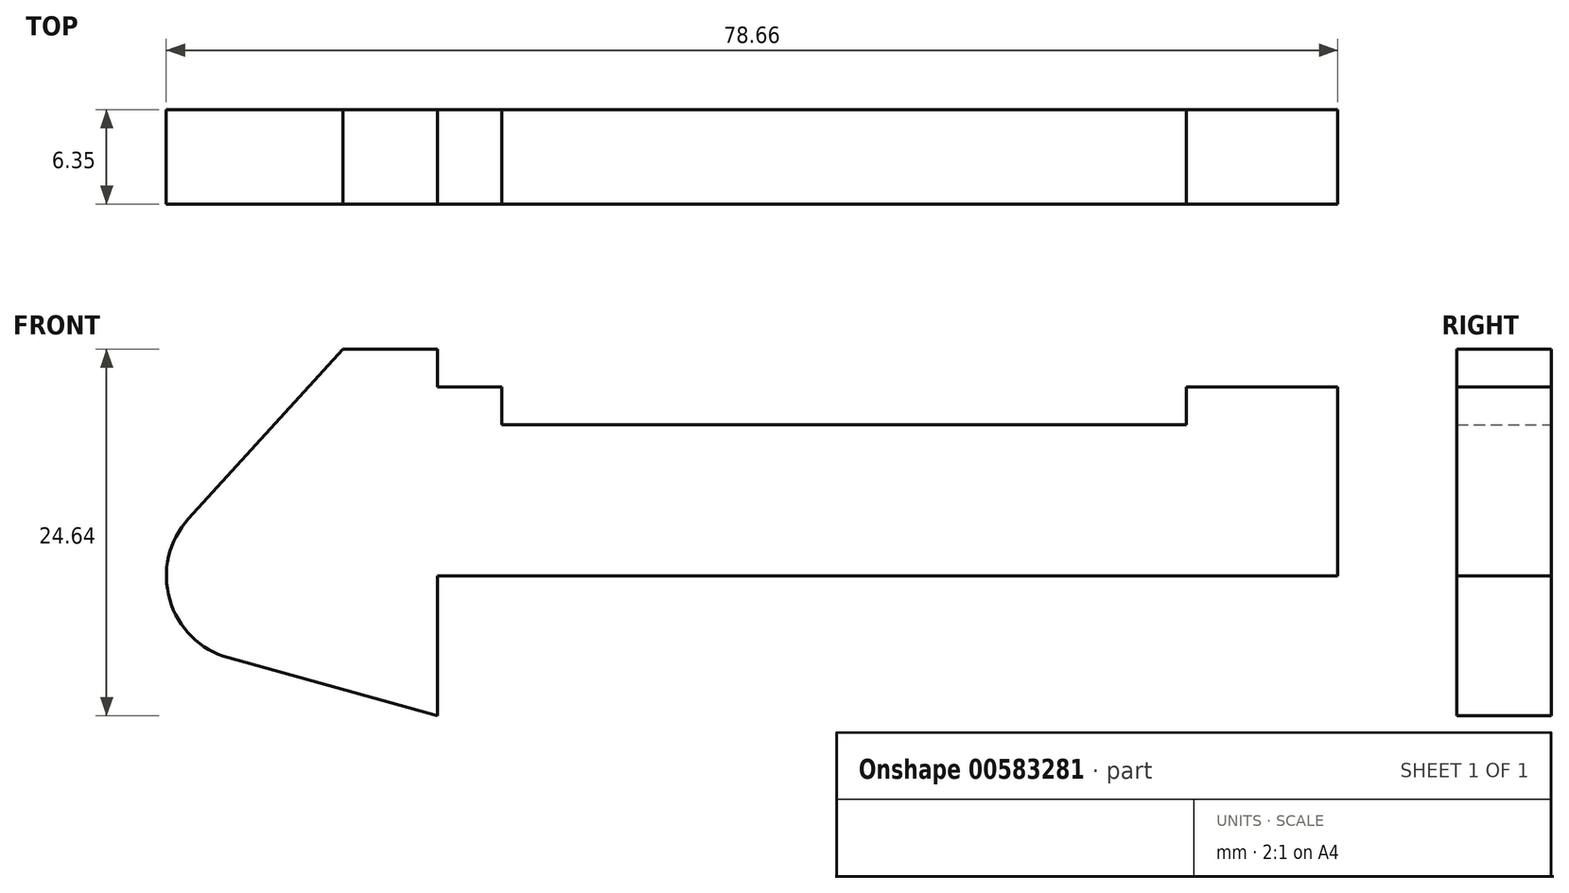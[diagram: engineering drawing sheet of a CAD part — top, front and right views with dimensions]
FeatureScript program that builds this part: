
annotation { "Feature Type Name" : "Feature", "Feature Type Description" : "" }
export const myFeature = defineFeature(function(context is Context, id is Id, definition is map)
    precondition{}
    {
        {
            var Q0;
            Q0=qCreatedBy(makeId("Front.planeOp"),FACE);
            var sketch = newSketch(context, id + "F0", { "sketchPlane" : qUnion([Q0])});
            skLineSegment(sketch, "E0", {"start": v(0, 0) * mm, "end": v(0, 12.7) * mm});
            skLineSegment(sketch, "E1", {"start": v(0, 12.7) * mm, "end": v(10.16, 12.7) * mm});
            skLineSegment(sketch, "E2", {"start": v(10.16, 12.7) * mm, "end": v(10.16, 10.16) * mm});
            skLineSegment(sketch, "E3", {"start": v(10.16, 10.16) * mm, "end": v(56.13, 10.16) * mm});
            skLineSegment(sketch, "E4", {"start": v(56.13, 10.16) * mm, "end": v(56.13, 12.7) * mm});
            skLineSegment(sketch, "E5", {"start": v(56.13, 12.7) * mm, "end": v(66.3, 12.7) * mm});
            skLineSegment(sketch, "E6", {"start": v(66.3, 12.7) * mm, "end": v(66.3, 0) * mm});
            skLineSegment(sketch, "E7", {"start": v(66.3, 0) * mm, "end": v(0, 0) * mm});
            skLineSegment(sketch, "E8", {"start": v(5.84, 15.24) * mm, "end": v(-0.5, 15.24) * mm});
            skLineSegment(sketch, "E9", {"start": v(-0.5, 15.24) * mm, "end": v(-10.88, 3.85) * mm});
            skLineSegment(sketch, "E10", {"start": v(0, 0) * mm, "end": v(-6.65, 0) * mm});
            skCircle(sketch, "E11", {"center": v(-6.65, 0) * mm, "radius": 5.72 * mm});
            skCircle(sketch, "E12", {"center": v(-6.65, 0) * mm, "radius": 3.18 * mm});
            skLineSegment(sketch, "E13", {"start": v(5.84, 15.24) * mm, "end": v(5.84, -9.4) * mm});
            skLineSegment(sketch, "E14", {"start": v(5.84, -9.4) * mm, "end": v(-8.18, -5.5) * mm});
            skSolve(sketch);
        }
        {
            var Q0;
            {var subQ0=sQuery(id+"F0.wireOp",EDGE,"E2");Q0=makeQuery(id+"F0.imprint","IMPRINT",FACE,{"disambiguationData":[TD([[makeQuery(id+"F0.imprint","IMPRINT",EDGE,{"derivedFrom":subQ0}),-1.0]])]});}
            var Q1;
            {var subQ0=sQuery(id+"F0.wireOp",EDGE,"E0");Q1=makeQuery(id+"F0.imprint","IMPRINT",FACE,{"disambiguationData":[TD([[makeQuery(id+"F0.imprint","IMPRINT",EDGE,{"derivedFrom":subQ0}),-1.0]])]});}
            var Q2;
            {var subQ1=sQuery(id+"F0.wireOp",EDGE,"E0");Q2=makeQuery(id+"F0.imprint","IMPRINT",FACE,{"disambiguationData":[TD([[makeQuery(id+"F0.imprint","IMPRINT",EDGE,{"derivedFrom":subQ1}),1.0]])]});}
            var Q3;
            {var subQ5=sQuery(id+"F0.wireOp",EDGE,"E12");Q3=makeQuery(id+"F0.imprint","IMPRINT",FACE,{"disambiguationData":[TD([[makeQuery(id+"F0.imprint","IMPRINT",EDGE,{"derivedFrom":subQ5}),-1.0]])]});}
            var Q4;
            {var subQ0=sQuery(id+"F0.wireOp",EDGE,"E12");Q4=makeQuery(id+"F0.imprint","IMPRINT",FACE,{"disambiguationData":[TD([[makeQuery(id+"F0.imprint","IMPRINT",EDGE,{"derivedFrom":subQ0}),1.0]])]});}
            var Q5;
            {var subQ0=sQuery(id+"F0.wireOp",EDGE,"E14");Q5=makeQuery(id+"F0.imprint","IMPRINT",FACE,{"disambiguationData":[TD([[makeQuery(id+"F0.imprint","IMPRINT",EDGE,{"derivedFrom":subQ0}),-1.0]])]});}
            extrude(context, id + "F1", {"entities" : qUnion([Q0, Q1, Q2, Q3, Q4, Q5]), "depth" : 6.35 * mm, "offsetDistance" : 25.4 * mm});
        }
    });
